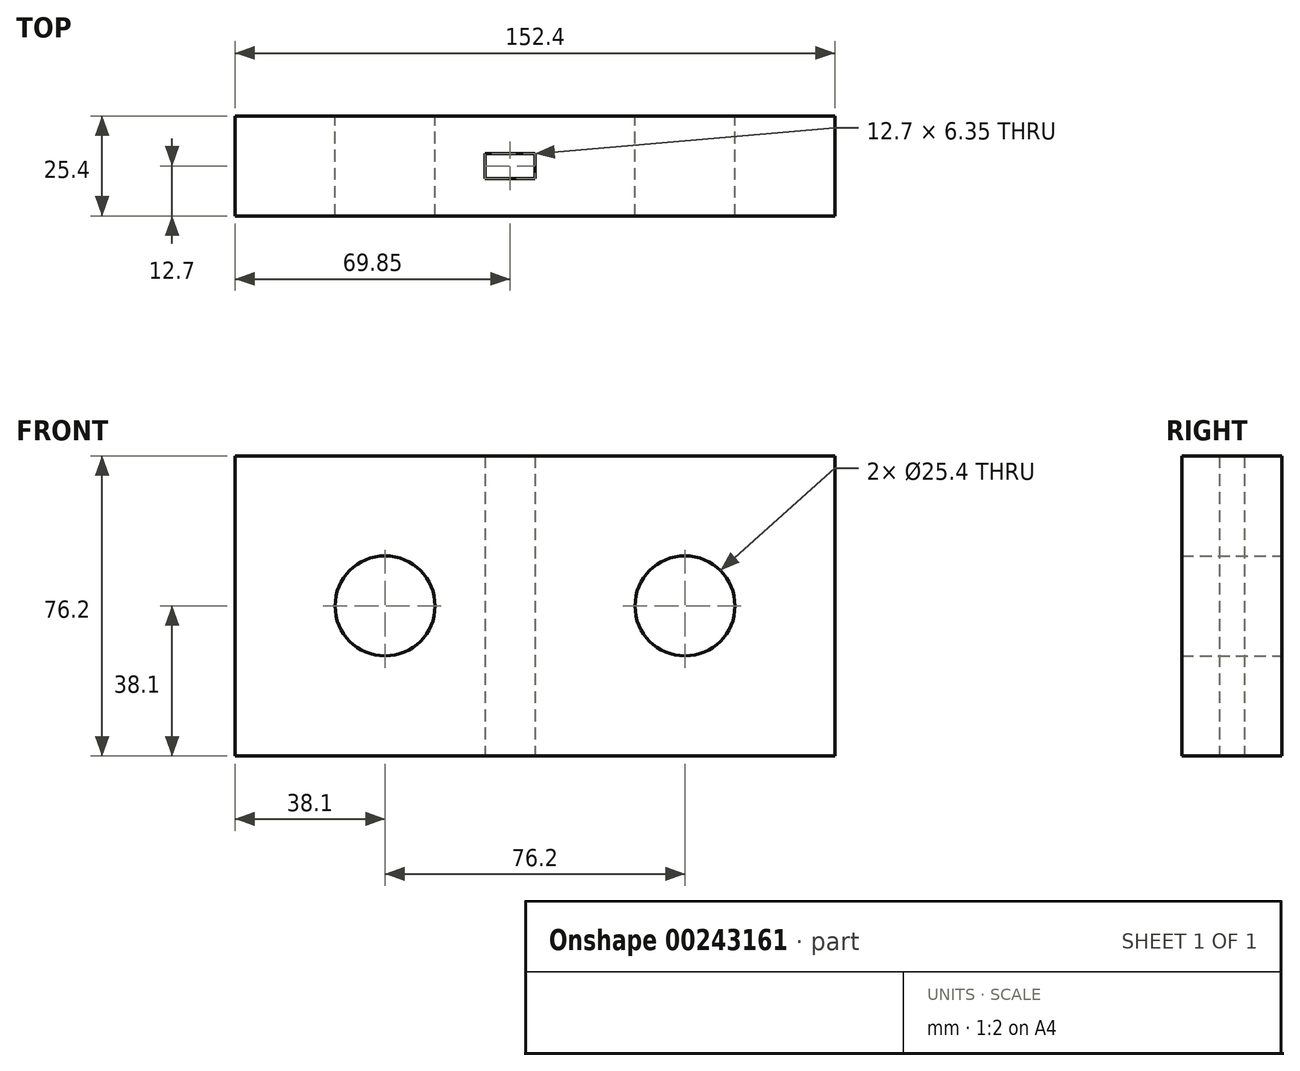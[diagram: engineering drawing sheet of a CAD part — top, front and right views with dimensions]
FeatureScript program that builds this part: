
annotation { "Feature Type Name" : "Feature", "Feature Type Description" : "" }
export const myFeature = defineFeature(function(context is Context, id is Id, definition is map)
    precondition{}
    {
        {
            var Q0;
            Q0=qCreatedBy(makeId("Front.planeOp"),FACE);
            var sketch = newSketch(context, id + "F0", { "sketchPlane" : qUnion([Q0])});
            skLineSegment(sketch, "E0.bottom", {"start": v(-76.2, 38.1) * mm, "end": v(76.2, 38.1) * mm});
            skLineSegment(sketch, "E0.top", {"start": v(-76.2, -38.1) * mm, "end": v(76.2, -38.1) * mm});
            skLineSegment(sketch, "E0.left", {"start": v(-76.2, 38.1) * mm, "end": v(-76.2, -38.1) * mm});
            skLineSegment(sketch, "E0.right", {"start": v(76.2, 38.1) * mm, "end": v(76.2, -38.1) * mm});
            skPoint(sketch, "E0.middle", {"position": v(0, 0) * mm});
            skLineSegment(sketch, "E1", {"start": v(0, 0) * mm, "end": v(-38.1, 0) * mm});
            skLineSegment(sketch, "E2", {"start": v(0, 0) * mm, "end": v(38.1, 0) * mm});
            skCircle(sketch, "E3", {"center": v(-38.1, 0) * mm, "radius": 12.7 * mm});
            skCircle(sketch, "E4", {"center": v(38.1, 0) * mm, "radius": 12.7 * mm});
            skSolve(sketch);
        }
        {
            var Q0;
            Q0=qCreatedBy(makeId("Top.planeOp"),FACE);
            var sketch = newSketch(context, id + "F1", { "sketchPlane" : qUnion([Q0])});
            skLineSegment(sketch, "E5.bottom", {"start": v(0, -9.53) * mm, "end": v(-12.7, -9.53) * mm});
            skLineSegment(sketch, "E5.top", {"start": v(0, -15.87) * mm, "end": v(-12.7, -15.87) * mm});
            skLineSegment(sketch, "E5.left", {"start": v(0, -9.53) * mm, "end": v(0, -15.88) * mm});
            skLineSegment(sketch, "E5.right", {"start": v(-12.7, -9.53) * mm, "end": v(-12.7, -15.87) * mm});
            skSolve(sketch);
        }
        {
            var Q0;
            Q0 = qSketchRegion(id + "F0", true);
            extrude(context, id + "F2", {"entities" : qUnion([Q0]), "depth" : 25.4 * mm});
        }
        {
            var Q0;
            Q0 = qSketchRegion(id + "F1", true);
            extrude(context, id + "F3", {"entities" : qUnion([Q0]), "operationType" : NewBodyOperationType.REMOVE, "endBound" : BoundingType.SYMMETRIC, "depth" : 76.2 * mm});
        }
    });
